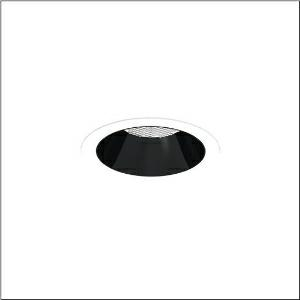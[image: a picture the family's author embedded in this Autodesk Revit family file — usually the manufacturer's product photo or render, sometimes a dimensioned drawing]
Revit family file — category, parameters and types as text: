
# Revit family: lunis_21_l_51db17ed91c
name_source: partatom
category: Lighting Fixtures
units: mm (PartAtom-declared; Revit-internal decimal feet)

## family parameters
Cut with Voids When Loaded = No
Host = Face
Light Source = No
Part Type = Normal
Room Calculation Point = No
Round Connector Dimension = Use Diameter
Shared = No

## types (1)
- --- (1 x LED, 3430 lm, 25.4 W, 6500K)
    Apparent Load = 25 VA
    CIE Flux Codes = 93 100 100 100 100
    Color Rendering = 80
    Color Temperature = 6500K
    Default Elevation = 1800 mm
    Description = Lunis 21,  L, downlight, light control with lens, of PMMA, anti glare with reflector, of PC, light emission: direct distribution, LED rated luminous flux: 1.790lm, light colour: 830/840/865, with terminal, 5-pole, mains connection: 220..240V, AC/DC, 0/50..60Hz, housing, round, of diecast aluminium, traffic white (RAL 9016), diameter: 165mm, clamping range: 1..40mm, protection rating (complete): IP20, protection rating (on room side): IP54, insulation class (complete): insulation class II (safety insulation), certification: CE, impact resistance: IK03, packaging unit: 1 piece
    Height = 0 mm  [stored 0 ft]
    Lamp = 1 x LED
    Lamp Light Flux = 3430 lm
    Lamp Power = 25.4 W
    Lamp count = 1
    Length = 165 mm
    Luminous efficacy = 135 lm/W
    Manufacturer = Siteco
    ModVariant = No
    Model = 51DB17ED91C
    Mounting Place = Ceiling
    Mounting Type = Recessed
    Number of Poles = 1
    OnlyDefault = Yes
    Power Factor = 1
    Product Name = Lunis 21 L
    Product group = downlight
    ProductGroupID = 401
    Protection Class = Protection class II
    Protection Degree = IP 20
    RLX_Detail_Level = 1
    RLX_Emergency_Light_Flux = 0 lm
    RLX_Emergency_Type = 0
    RLX_Emergency_Type_DB = No
    RlxData = <blob elided: 18513 chars, md5=8cc16c32>
    Socket = socket
    Standby Power = 0 W
    System Light Flux = 3430 lm
    System Power = 25 W
    Type Comments = individual setting: colour temperature 6500K, luminous flux: 100 % | (ON | ON | OFF | OFF) | 700 mA
    Type Image = l_1291094.jpg
    URL = http://relux.com
    VarID = @adj_039901
    Voltage = 0 V
    Weight = 0.00 kg
    Width = 0 mm  [stored 0 ft]

note: [stored X ft] marks values corroborated as IEEE doubles in the binary element streams (Revit-internal decimal feet)

## geometry (parser evidence)
native form markers: Blend x4, Sweep x12
no freeform markers — native parametric forms only
